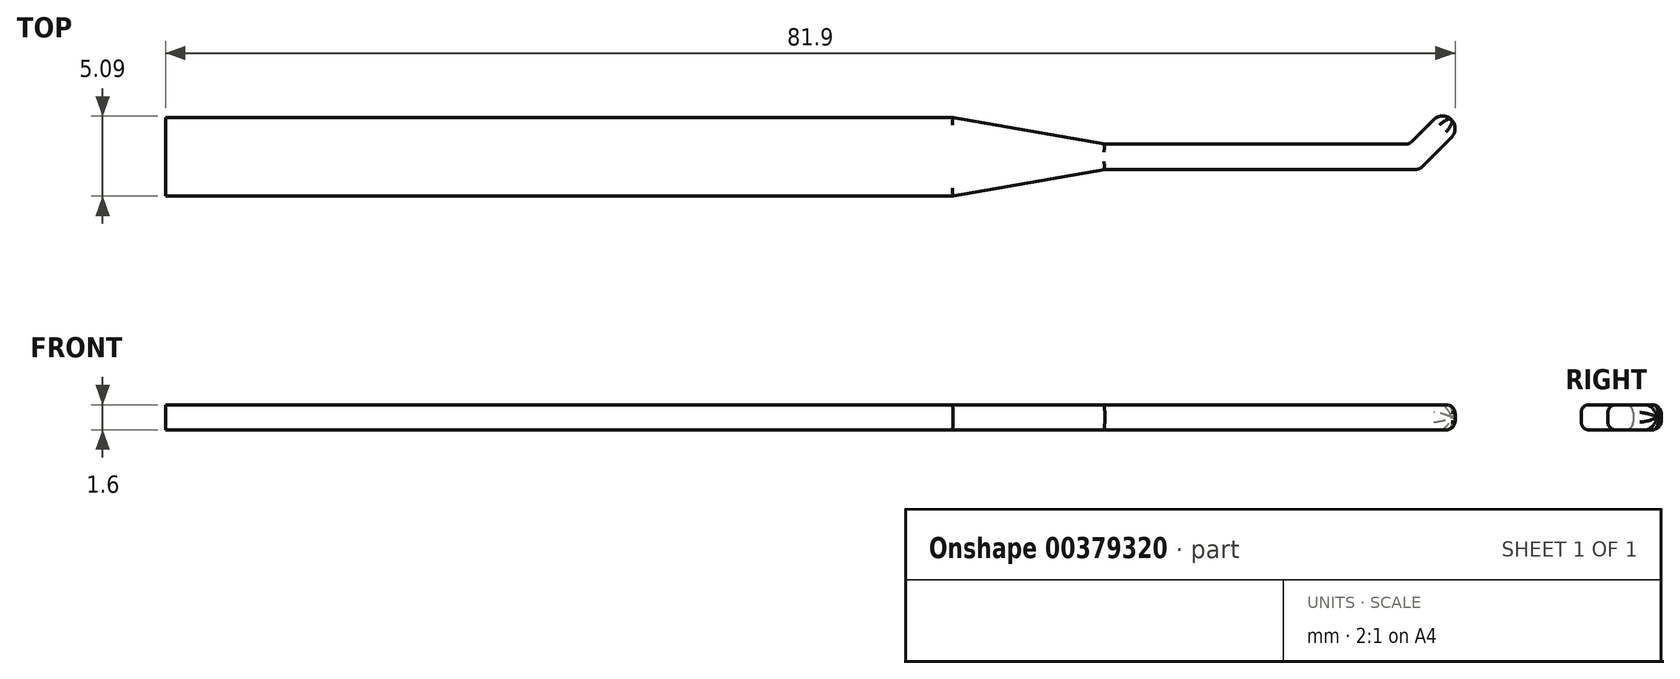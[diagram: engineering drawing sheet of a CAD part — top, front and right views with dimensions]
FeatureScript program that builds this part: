
annotation { "Feature Type Name" : "Feature", "Feature Type Description" : "" }
export const myFeature = defineFeature(function(context is Context, id is Id, definition is map)
    precondition{}
    {
        {
            var Q0;
            Q0=qCreatedBy(makeId("Top.planeOp"),FACE);
            var sketch = newSketch(context, id + "F0", { "sketchPlane" : qUnion([Q0])});
            skLineSegment(sketch, "E0", {"start": v(-10, 0) * mm, "end": v(10, 0) * mm});
            skLineSegment(sketch, "E1", {"start": v(10, 0) * mm, "end": v(12.59, 2.59) * mm});
            skLineSegment(sketch, "E2", {"start": v(12.59, 2.59) * mm, "end": v(11.46, 3.72) * mm});
            skLineSegment(sketch, "E3", {"start": v(11.46, 3.72) * mm, "end": v(9.34, 1.6) * mm});
            skLineSegment(sketch, "E4", {"start": v(9.34, 1.6) * mm, "end": v(-10, 1.6) * mm});
            skLineSegment(sketch, "E5", {"start": v(-10, 1.6) * mm, "end": v(-19.64, 3.3) * mm});
            skLineSegment(sketch, "E6", {"start": v(-19.64, 3.3) * mm, "end": v(-69.64, 3.3) * mm});
            skLineSegment(sketch, "E7", {"start": v(-69.64, 3.3) * mm, "end": v(-69.64, -1.7) * mm});
            skLineSegment(sketch, "E8", {"start": v(-69.64, -1.7) * mm, "end": v(-19.64, -1.7) * mm});
            skLineSegment(sketch, "E9", {"start": v(-19.64, -1.7) * mm, "end": v(-10, 0) * mm});
            skSolve(sketch);
        }
        {
            var Q0;
            Q0 = qSketchRegion(id + "F0", true);
            extrude(context, id + "F1", {"entities" : qUnion([Q0]), "depth" : 1.6 * mm});
        }
        {
            var Q0;
            Q0=makeQuery(id+"F1.opExtrude","SWEPT_EDGE",EDGE,{"disambiguationData":[OSD([sQuery(id+"F0.wireOp",EDGE,"E1"),sQuery(id+"F0.wireOp",EDGE,"E2")])]});
            var Q1;
            Q1=makeQuery(id+"F1.opExtrude","CAP_EDGE",EDGE,{"disambiguationData":[OSD([sQuery(id+"F0.wireOp",EDGE,"E2")])],"isStart":false});
            var Q2;
            Q2=makeQuery(id+"F1.opExtrude","SWEPT_EDGE",EDGE,{"disambiguationData":[OSD([sQuery(id+"F0.wireOp",EDGE,"E2"),sQuery(id+"F0.wireOp",EDGE,"E3")])]});
            var Q3;
            Q3=makeQuery(id+"F1.opExtrude","CAP_EDGE",EDGE,{"disambiguationData":[OSD([sQuery(id+"F0.wireOp",EDGE,"E2")])],"isStart":true});
            fillet(context, id + "F2", {"entities" : qUnion([Q0, Q1, Q2, Q3]), "radius" : 0.8 * mm, "tangentPropagation" : true, "allowEdgeOverflow" : false});
        }
        {
            var Q0;
            Q0=makeQuery(id+"F1.opExtrude","CAP_EDGE",EDGE,{"disambiguationData":[OSD([sQuery(id+"F0.wireOp",EDGE,"E1")])],"isStart":false});
            var Q1;
            Q1=makeQuery(id+"F1.opExtrude","CAP_EDGE",EDGE,{"disambiguationData":[OSD([sQuery(id+"F0.wireOp",EDGE,"E1")])],"isStart":true});
            var Q2;
            Q2=makeQuery(id+"F1.opExtrude","CAP_EDGE",EDGE,{"disambiguationData":[OSD([sQuery(id+"F0.wireOp",EDGE,"E3")])],"isStart":false});
            var Q3;
            Q3=makeQuery(id+"F1.opExtrude","CAP_EDGE",EDGE,{"disambiguationData":[OSD([sQuery(id+"F0.wireOp",EDGE,"E3")])],"isStart":true});
            var Q4;
            Q4=makeQuery(id+"F1.opExtrude","CAP_EDGE",EDGE,{"disambiguationData":[OSD([sQuery(id+"F0.wireOp",EDGE,"E4")])],"isStart":true});
            var Q5;
            Q5=makeQuery(id+"F1.opExtrude","CAP_EDGE",EDGE,{"disambiguationData":[OSD([sQuery(id+"F0.wireOp",EDGE,"E0")])],"isStart":true});
            var Q6;
            Q6=makeQuery(id+"F1.opExtrude","SWEPT_EDGE",EDGE,{"disambiguationData":[OSD([sQuery(id+"F0.wireOp",EDGE,"E3"),sQuery(id+"F0.wireOp",EDGE,"E4")])]});
            var Q7;
            Q7=makeQuery(id+"F1.opExtrude","CAP_EDGE",EDGE,{"disambiguationData":[OSD([sQuery(id+"F0.wireOp",EDGE,"E4")])],"isStart":false});
            var Q8;
            Q8=makeQuery(id+"F1.opExtrude","CAP_EDGE",EDGE,{"disambiguationData":[OSD([sQuery(id+"F0.wireOp",EDGE,"E0")])],"isStart":false});
            var Q9;
            Q9=makeQuery(id+"F1.opExtrude","SWEPT_EDGE",EDGE,{"disambiguationData":[OSD([sQuery(id+"F0.wireOp",EDGE,"E0"),sQuery(id+"F0.wireOp",EDGE,"E1")])]});
            var Q10;
            Q10=makeQuery(id+"F1.opExtrude","CAP_EDGE",EDGE,{"disambiguationData":[OSD([sQuery(id+"F0.wireOp",EDGE,"E9")])],"isStart":true});
            var Q11;
            Q11=makeQuery(id+"F1.opExtrude","CAP_EDGE",EDGE,{"disambiguationData":[OSD([sQuery(id+"F0.wireOp",EDGE,"E8")])],"isStart":true});
            var Q12;
            Q12=makeQuery(id+"F1.opExtrude","CAP_EDGE",EDGE,{"disambiguationData":[OSD([sQuery(id+"F0.wireOp",EDGE,"E5")])],"isStart":true});
            var Q13;
            Q13=makeQuery(id+"F1.opExtrude","CAP_EDGE",EDGE,{"disambiguationData":[OSD([sQuery(id+"F0.wireOp",EDGE,"E6")])],"isStart":true});
            var Q14;
            Q14=makeQuery(id+"F1.opExtrude","CAP_EDGE",EDGE,{"disambiguationData":[OSD([sQuery(id+"F0.wireOp",EDGE,"E8")])],"isStart":false});
            var Q15;
            Q15=makeQuery(id+"F1.opExtrude","CAP_EDGE",EDGE,{"disambiguationData":[OSD([sQuery(id+"F0.wireOp",EDGE,"E9")])],"isStart":false});
            var Q16;
            Q16=makeQuery(id+"F1.opExtrude","CAP_EDGE",EDGE,{"disambiguationData":[OSD([sQuery(id+"F0.wireOp",EDGE,"E6")])],"isStart":false});
            var Q17;
            Q17=makeQuery(id+"F1.opExtrude","CAP_EDGE",EDGE,{"disambiguationData":[OSD([sQuery(id+"F0.wireOp",EDGE,"E5")])],"isStart":false});
            fillet(context, id + "F3", {"entities" : qUnion([Q0, Q1, Q2, Q3, Q4, Q5, Q6, Q7, Q8, Q9, Q10, Q11, Q12, Q13, Q14, Q15, Q16, Q17]), "radius" : 0.5 * mm, "tangentPropagation" : true, "allowEdgeOverflow" : false});
        }
    });
